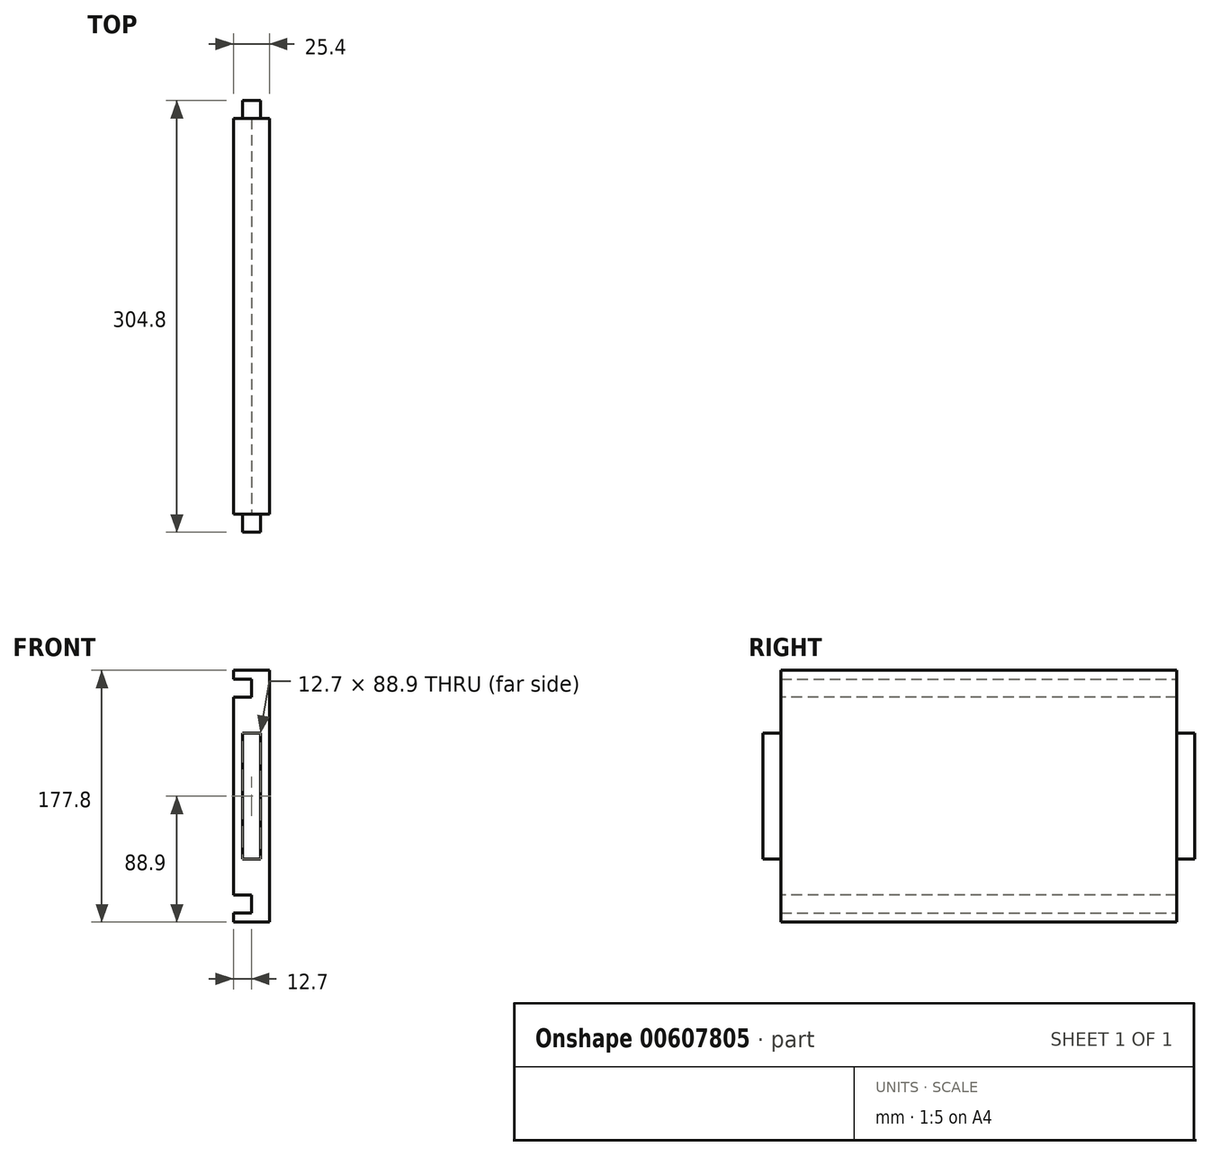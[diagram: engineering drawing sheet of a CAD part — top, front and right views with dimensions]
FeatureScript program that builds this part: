
annotation { "Feature Type Name" : "Feature", "Feature Type Description" : "" }
export const myFeature = defineFeature(function(context is Context, id is Id, definition is map)
    precondition{}
    {
        {
            var Q0;
            Q0=qCreatedBy(makeId("Right.planeOp"),FACE);
            var sketch = newSketch(context, id + "F0", { "sketchPlane" : qUnion([Q0])});
            skLineSegment(sketch, "E0.bottom", {"start": v(0, 0) * mm, "end": v(-279.4, 0) * mm});
            skLineSegment(sketch, "E0.top", {"start": v(0, 177.8) * mm, "end": v(-279.4, 177.8) * mm});
            skLineSegment(sketch, "E0.left", {"start": v(0, 0) * mm, "end": v(0, 177.8) * mm});
            skLineSegment(sketch, "E0.right", {"start": v(-279.4, 0) * mm, "end": v(-279.4, 177.8) * mm});
            skSolve(sketch);
        }
        {
            var Q0;
            Q0=makeQuery(id+"F0.imprint","IMPRINT",FACE,{"disambiguationData":[TD([[makeQuery(id+"F0.imprint","IMPRINT",EDGE,{"derivedFrom":sQuery(id+"F0.wireOp",EDGE,"E0.bottom")}),-1.0]])]});
            extrude(context, id + "F1", {"entities" : qUnion([Q0]), "depth" : 25.4 * mm, "offsetDistance" : 25.4 * mm});
        }
        {
            var Q0;
            Q0=makeQuery(id+"F1.opExtrude","CAP_FACE",FACE,{"disambiguationData":[OSD([sQuery(id+"F0.wireOp",EDGE,"E0.bottom"),sQuery(id+"F0.wireOp",EDGE,"E0.top"),sQuery(id+"F0.wireOp",EDGE,"E0.left"),sQuery(id+"F0.wireOp",EDGE,"E0.right")])],"isStart":true});
            var sketch = newSketch(context, id + "F2", { "sketchPlane" : qUnion([Q0])});
            skLineSegment(sketch, "E1", {"start": v(0, 0) * mm, "end": v(0, 6.35) * mm});
            skLineSegment(sketch, "E2", {"start": v(0, 19.05) * mm, "end": v(0, 6.35) * mm});
            skLineSegment(sketch, "E3", {"start": v(0, 19.05) * mm, "end": v(279.4, 19.05) * mm});
            skLineSegment(sketch, "E4", {"start": v(279.4, 19.05) * mm, "end": v(279.4, 6.35) * mm});
            skLineSegment(sketch, "E5", {"start": v(279.4, 6.35) * mm, "end": v(0, 6.35) * mm});
            skSolve(sketch);
        }
        {
            var Q0;
            Q0=makeQuery(id+"F2.imprint","IMPRINT",FACE,{"disambiguationData":[TD([[makeQuery(id+"F2.imprint","IMPRINT",EDGE,{"derivedFrom":sQuery(id+"F2.wireOp",EDGE,"E2")}),-1.0]])]});
            extrude(context, id + "F3", {"entities" : qUnion([Q0]), "operationType" : NewBodyOperationType.REMOVE, "oppositeDirection" : true, "depth" : 12.7 * mm, "offsetDistance" : 25.4 * mm});
        }
        {
            var Q0;
            {var subQ0=sQuery(id+"F0.wireOp",EDGE,"E0.top");var subQ1=sQuery(id+"F0.wireOp",EDGE,"E0.left");var subQ2=sQuery(id+"F0.wireOp",EDGE,"E0.right");Q0=makeQuery(id+"F3.boolean.opBoolean","SPLIT",FACE,{"disambiguationData":[TD([makeQuery(id+"F1.opExtrude","SWEPT_FACE",FACE,{"disambiguationData":[OSD([subQ0])]})])],"derivedFrom":makeQuery(id+"F1.opExtrude","CAP_FACE",FACE,{"disambiguationData":[OSD([sQuery(id+"F0.wireOp",EDGE,"E0.bottom"),subQ0,subQ1,subQ2])],"isStart":true})});}
            var sketch = newSketch(context, id + "F4", { "sketchPlane" : qUnion([Q0])});
            skLineSegment(sketch, "E6", {"start": v(0, 177.8) * mm, "end": v(0, 171.45) * mm});
            skLineSegment(sketch, "E7", {"start": v(0, 171.45) * mm, "end": v(0, 158.75) * mm});
            skLineSegment(sketch, "E8", {"start": v(0, 158.75) * mm, "end": v(279.4, 158.75) * mm});
            skLineSegment(sketch, "E9", {"start": v(279.4, 158.75) * mm, "end": v(279.4, 171.45) * mm});
            skLineSegment(sketch, "E10", {"start": v(279.4, 171.45) * mm, "end": v(0, 171.45) * mm});
            skSolve(sketch);
        }
        {
            var Q0;
            Q0=makeQuery(id+"F4.imprint","IMPRINT",FACE,{"disambiguationData":[TD([[makeQuery(id+"F4.imprint","IMPRINT",EDGE,{"derivedFrom":sQuery(id+"F4.wireOp",EDGE,"E7")}),-1.0]])]});
            extrude(context, id + "F5", {"entities" : qUnion([Q0]), "operationType" : NewBodyOperationType.REMOVE, "oppositeDirection" : true, "depth" : 12.7 * mm, "offsetDistance" : 25.4 * mm});
        }
        {
            var Q0;
            Q0=makeQuery(id+"F1.opExtrude","SWEPT_FACE",FACE,{"disambiguationData":[OSD([sQuery(id+"F0.wireOp",EDGE,"E0.left")])]});
            var sketch = newSketch(context, id + "F6", { "sketchPlane" : qUnion([Q0])});
            skLineSegment(sketch, "E11", {"start": v(-25.4, 177.8) * mm, "end": v(-19.05, 177.8) * mm});
            skLineSegment(sketch, "E12", {"start": v(-19.05, 177.8) * mm, "end": v(-19.05, 133.35) * mm});
            skLineSegment(sketch, "E13", {"start": v(-19.05, 133.35) * mm, "end": v(-6.35, 133.35) * mm});
            skLineSegment(sketch, "E14", {"start": v(-6.35, 133.35) * mm, "end": v(-6.35, 44.45) * mm});
            skLineSegment(sketch, "E15", {"start": v(-6.35, 44.45) * mm, "end": v(-19.05, 44.45) * mm});
            skLineSegment(sketch, "E16", {"start": v(-19.05, 44.45) * mm, "end": v(-19.05, 133.35) * mm});
            skSolve(sketch);
        }
        {
            var Q0;
            Q0=makeQuery(id+"F6.imprint","IMPRINT",FACE,{"disambiguationData":[TD([[makeQuery(id+"F6.imprint","IMPRINT",EDGE,{"derivedFrom":sQuery(id+"F6.wireOp",EDGE,"E13")}),-1.0]])]});
            extrude(context, id + "F7", {"entities" : qUnion([Q0]), "operationType" : NewBodyOperationType.ADD, "depth" : 12.7 * mm, "offsetDistance" : 25.4 * mm});
        }
        {
            var Q0;
            Q0=makeQuery(id+"F1.opExtrude","SWEPT_FACE",FACE,{"disambiguationData":[OSD([sQuery(id+"F0.wireOp",EDGE,"E0.right")])]});
            var sketch = newSketch(context, id + "F8", { "sketchPlane" : qUnion([Q0])});
            skLineSegment(sketch, "E17", {"start": v(25.4, 177.8) * mm, "end": v(19.05, 177.8) * mm});
            skLineSegment(sketch, "E18", {"start": v(19.05, 177.8) * mm, "end": v(19.05, 133.35) * mm});
            skLineSegment(sketch, "E19", {"start": v(19.05, 133.35) * mm, "end": v(19.05, 44.45) * mm});
            skLineSegment(sketch, "E20", {"start": v(19.05, 44.45) * mm, "end": v(6.35, 44.45) * mm});
            skLineSegment(sketch, "E21", {"start": v(6.35, 44.45) * mm, "end": v(6.35, 133.35) * mm});
            skLineSegment(sketch, "E22", {"start": v(6.35, 133.35) * mm, "end": v(19.05, 133.35) * mm});
            skSolve(sketch);
        }
        {
            var Q0;
            Q0=makeQuery(id+"F8.imprint","IMPRINT",FACE,{"disambiguationData":[TD([[makeQuery(id+"F8.imprint","IMPRINT",EDGE,{"derivedFrom":sQuery(id+"F8.wireOp",EDGE,"E19")}),-1.0]])]});
            extrude(context, id + "F9", {"entities" : qUnion([Q0]), "operationType" : NewBodyOperationType.ADD, "depth" : 12.7 * mm, "offsetDistance" : 25.4 * mm});
        }
    });
